# Revit family: Plumbing-Pipe_DWV
name_source: partatom
category: Plumbing Fixtures
units: mm (PartAtom-declared; Revit-internal decimal feet)

## family parameters
Classification Number = 23.60.30.11.14
Cut with Voids When Loaded = No
Enable Cutting in Views = No
Maintain Annotation Orientation = No
Part Type = Normal
Room Calculation Point = No
Round Connector Dimension = Use Diameter
Shared = No

## types (18) — shared parameters
Assembly Code = D2030
CW Connection = No
Connection Type = Solvent Welded
Construction Details = http://www.arcat.com
Default Elevation = 0' - 0"
Green Building-LEED = http://www.arcat.com
HW Connection = No
Keynote = 15000
Manufacturer = Generic
Manufacturer Fax = (203) 929-2444
Manufacturer Website = http://www.arcat.com
Model = Generic
Product Data = http://www.arcat.com
Product Properties = http://www.arcat.com
Specification = http://www.arcat.com
Vent Connection = Yes
Wall Thickness = 0' - 0 3/16"
Waste Connection = Yes
zero-valued in all types: Expected Lifespan (Years), Maintenance Schedule (Months), Warranty Duration (Years)

## per-type parameters (varying)
| type | ASTM Standard | Description | Drain Connection Type | Pipe ID | Pipe Material | Pipe OD | PipeIrad | PipeOrad |
| 2" Sch 40 | D1784 / D1785 | Schedule 40 PVC Pipe | Plumbing-Connector : Weld-Weld -PVC-PVC 2 | 0' - 1 5/8" | ARCAT - PVC - Schedule 40 | 0' - 2" | 0' - 0 13/16" | 0' - 1" |
| 1-1/2" Sch 40 | D1784 / D1785 | Schedule 40 PVC Pipe | Plumbing-Connector : Weld-Weld -PVC-PVC 150 | 0' - 1 1/8" | ARCAT - PVC - Schedule 40 | 0' - 1 1/2" | 0' - 0 9/16" | 0' - 0 3/4" |
| 1-1/4" Sch 40 | D1784 / D1785 | Schedule 40 PVC Pipe | Plumbing-Connector : Weld-Weld -PVC-PVC 125 | 0' - 0 7/8" | ARCAT - PVC - Schedule 40 | 0' - 1 1/4" | 0' - 0 7/16" | 0' - 0 5/8" |
| 1" Sch 40 | D1784 / D1785 | Schedule 40 PVC Pipe | Plumbing-Connector : Weld-Weld -PVC-PVC 125 | 0' - 0 5/8" | ARCAT - PVC - Schedule 40 | 0' - 1" | 0' - 0 5/16" | 0' - 0 1/2" |
| 3" Sch 40 | D1784 / D1785 | Schedule 40 PVC Pipe | Plumbing-Connector : Weld-Weld -PVC-PVC 3 | 0' - 2 5/8" | ARCAT - PVC - Schedule 40 | 0' - 3" | 0' - 1 5/16" | 0' - 1 1/2" |
| 4" sch 40 | D1784 / D1785 | Schedule 40 PVC Pipe | Plumbing-Connector : Weld-Weld -PVC-PVC 4 | 0' - 3 5/8" | ARCAT - PVC - Schedule 40 | 0' - 4" | 0' - 1 13/16" | 0' - 2" |
| 1-1/2" Sch 80 | D1784 / D1785 | Schedule 80 PVC Pipe | Plumbing-Connector : Weld-Weld -PVC-PVC 150 | 0' - 1 1/8" | ARCAT - PVC - Schedule 80 | 0' - 1 1/2" | 0' - 0 9/16" | 0' - 0 3/4" |
| 4" sch 80 | D1784 / D1785 | Schedule 80 PVC Pipe | Plumbing-Connector : Weld-Weld -PVC-PVC 4 | 0' - 3 5/8" | ARCAT - PVC - Schedule 80 | 0' - 4" | 0' - 1 13/16" | 0' - 2" |
| 3" sch 80 | D1784 / D1785 | Schedule 80 PVC Pipe | Plumbing-Connector : Weld-Weld -PVC-PVC 3 | 0' - 3 5/8" | ARCAT - PVC - Schedule 80 | 0' - 4" | 0' - 1 13/16" | 0' - 2" |
| 2" Sch 80 | D1784 / D1785 | Schedule 80 PVC Pipe | Plumbing-Connector : Weld-Weld -PVC-PVC 2 | 0' - 1 5/8" | ARCAT - PVC - Schedule 80 | 0' - 2" | 0' - 0 13/16" | 0' - 1" |
| 1" Sch 80 | D1784 / D1785 | Schedule 80 PVC Pipe | Plumbing-Connector : Weld-Weld -PVC-PVC 125 | 0' - 0 5/8" | ARCAT - PVC - Schedule 80 | 0' - 1" | 0' - 0 5/16" | 0' - 0 1/2" |
| 1-1/4" Sch 80 | D1784 / D1785 | Schedule 80 PVC Pipe | Plumbing-Connector : Weld-Weld -PVC-PVC 125 | 0' - 0 7/8" | ARCAT - PVC - Schedule 80 | 0' - 1 1/4" | 0' - 0 7/16" | 0' - 0 5/8" |
| 1-1/4" SDR | D1784 / D2241 | SDR PVC Pipe | Plumbing-Connector : Weld-Weld -PVC-PVC 125 | 0' - 0 7/8" | ARCAT - PVC - SDR | 0' - 1 1/4" | 0' - 0 7/16" | 0' - 0 5/8" |
| 2" SDR | D1784 / D2241 | SDR PVC Pipe | Plumbing-Connector : Weld-Weld -PVC-PVC 2 | 0' - 1 5/8" | ARCAT - PVC - SDR | 0' - 2" | 0' - 0 13/16" | 0' - 1" |
| 1-1/2" SDR | D1784 / D2241 | SDR PVC Pipe | Plumbing-Connector : Weld-Weld -PVC-PVC 150 | 0' - 1 1/8" | ARCAT - PVC - SDR | 0' - 1 1/2" | 0' - 0 9/16" | 0' - 0 3/4" |
| 3" SDR | D1784 / D2241 | SDR PVC Pipe | Plumbing-Connector : Weld-Weld -PVC-PVC 3 | 0' - 3 5/8" | ARCAT - PVC - SDR | 0' - 4" | 0' - 1 13/16" | 0' - 2" |
| 4" SDR | D1784 / D2241 | SDR PVC Pipe | Plumbing-Connector : Weld-Weld -PVC-PVC 4 | 0' - 3 5/8" | ARCAT - PVC - SDR | 0' - 4" | 0' - 1 13/16" | 0' - 2" |
| 5" SDR | D1784 / D2241 | SDR PVC Pipe | Plumbing-Connector : Weld-Weld -PVC-PVC 4 | 0' - 4 5/8" | ARCAT - PVC - SDR | 0' - 5" | 0' - 2 5/16" | 0' - 2 1/2" |

## geometry (parser evidence)
native form markers: Sweep x6
no freeform markers — native parametric forms only
